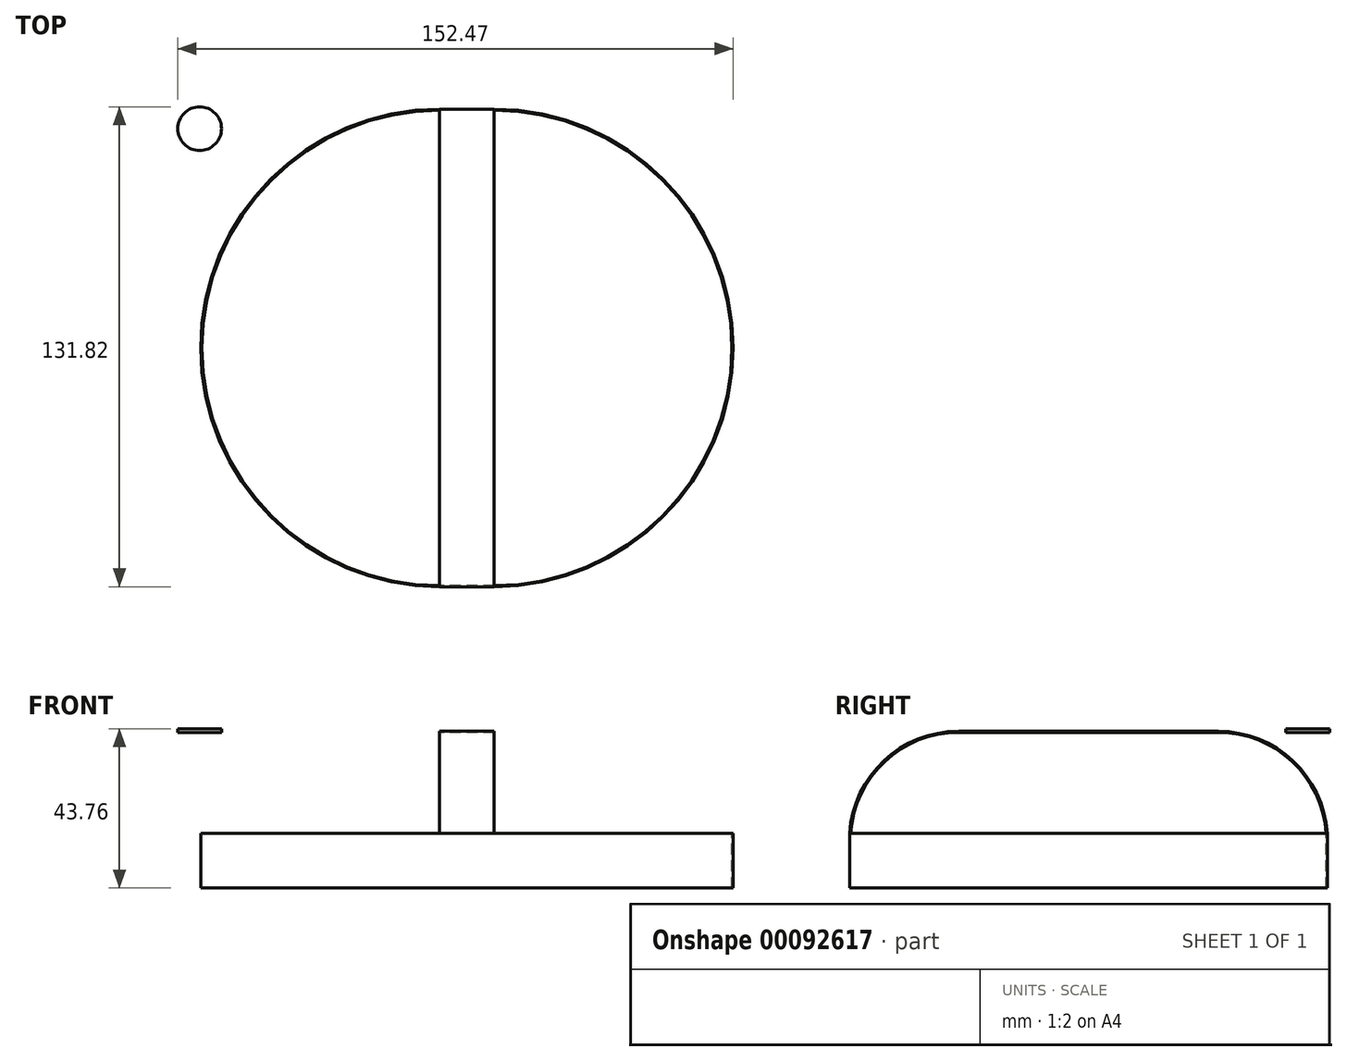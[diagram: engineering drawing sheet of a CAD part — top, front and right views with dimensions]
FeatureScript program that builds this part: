
annotation { "Feature Type Name" : "Feature", "Feature Type Description" : "" }
export const myFeature = defineFeature(function(context is Context, id is Id, definition is map)
    precondition{}
    {
        {
            var Q0;
            Q0=qCreatedBy(makeId("Right.planeOp"),FACE);
            var sketch = newSketch(context, id + "F0", { "sketchPlane" : qUnion([Q0])});
            skLineSegment(sketch, "E0", {"start": v(-35.65, 0) * mm, "end": v(35.65, 0) * mm});
            skArc(sketch, "E1", {"start": v(-35.65, 0) * mm, "mid": v(-55.95, -8.03) * mm, "end": v(-65.29, -27.76) * mm});
            skArc(sketch, "E2.MirrorCS", {"start": v(35.65, 0) * mm, "mid": v(55.95, -8.03) * mm, "end": v(65.29, -27.76) * mm});
            skArc(sketch, "E3.0", {"start": v(-35.65, 0.3) * mm, "mid": v(-56.17, -7.81) * mm, "end": v(-65.59, -27.76) * mm});
            skLineSegment(sketch, "E3.1", {"start": v(-35.65, 0.3) * mm, "end": v(35.65, 0.3) * mm});
            skArc(sketch, "E3.2", {"start": v(35.65, 0.3) * mm, "mid": v(56.17, -7.81) * mm, "end": v(65.59, -27.76) * mm});
            skLineSegment(sketch, "E4", {"start": v(-65.59, -27.76) * mm, "end": v(-65.29, -27.76) * mm});
            skLineSegment(sketch, "E5", {"start": v(65.29, -27.76) * mm, "end": v(65.59, -27.76) * mm});
            skSolve(sketch);
        }
        {
            var Q0;
            Q0 = qSketchRegion(id + "F0", true);
            extrude(context, id + "F1", {"entities" : qUnion([Q0]), "depth" : 15 * mm});
        }
        {
            var Q0;
            Q0=makeQuery(id+"F1.opExtrude","SWEPT_FACE",FACE,{"disambiguationData":[OSD([sQuery(id+"F0.wireOp",EDGE,"E5")])]});
            var sketch = newSketch(context, id + "F2", { "sketchPlane" : qUnion([Q0])});
            skLineSegment(sketch, "E6.0", {"start": v(15, -65.29) * mm, "end": v(0, -65.29) * mm});
            skLineSegment(sketch, "E6.1", {"start": v(15, -65.59) * mm, "end": v(0, -65.59) * mm});
            skLineSegment(sketch, "E7.0", {"start": v(15, 65.29) * mm, "end": v(0, 65.29) * mm});
            skLineSegment(sketch, "E7.1", {"start": v(15, 65.59) * mm, "end": v(0, 65.59) * mm});
            skArc(sketch, "E8", {"start": v(0, 65.29) * mm, "mid": v(-65.29, 0) * mm, "end": v(0, -65.29) * mm});
            skArc(sketch, "E9", {"start": v(0, 65.59) * mm, "mid": v(-65.59, 0) * mm, "end": v(0, -65.59) * mm});
            skLineSegment(sketch, "E10", {"start": v(7.5, 87.4) * mm, "end": v(7.5, -101.45) * mm, "construction": true});
            skArc(sketch, "E11.MirrorCS", {"start": v(15, 65.29) * mm, "mid": v(80.29, 0) * mm, "end": v(15, -65.29) * mm});
            skArc(sketch, "E12.MirrorCS", {"start": v(15, 65.59) * mm, "mid": v(80.59, 0) * mm, "end": v(15, -65.59) * mm});
            skSolve(sketch);
        }
        {
            var Q0;
            Q0 = qSketchRegion(id + "F2", true);
            extrude(context, id + "F3", {"entities" : qUnion([Q0]), "operationType" : NewBodyOperationType.ADD, "depth" : 15 * mm});
        }
        {
            var Q0;
            Q0=qCreatedBy(makeId("Top.planeOp"),FACE);
            var sketch = newSketch(context, id + "F4", { "sketchPlane" : qUnion([Q0])});
            skCircle(sketch, "E13", {"center": v(-65.88, 60.23) * mm, "radius": 6 * mm});
            skSolve(sketch);
        }
        {
            var Q0;
            Q0 = qSketchRegion(id + "F4", true);
            extrude(context, id + "F5", {"entities" : qUnion([Q0]), "depth" : 1 * mm});
        }
    });
